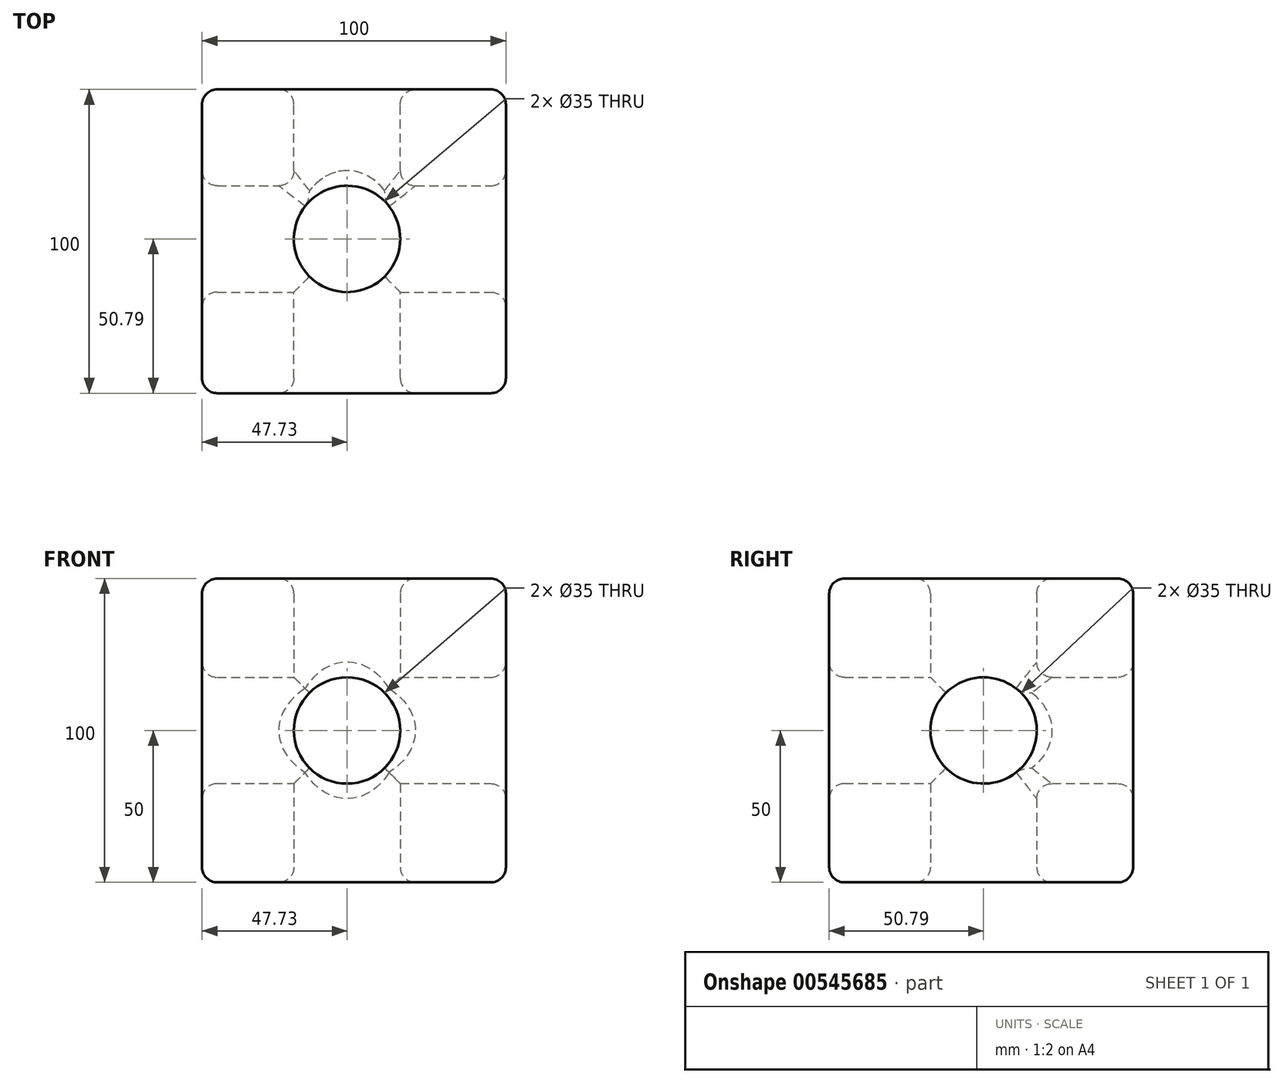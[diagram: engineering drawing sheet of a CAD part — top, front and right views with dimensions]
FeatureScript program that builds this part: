
annotation { "Feature Type Name" : "Feature", "Feature Type Description" : "" }
export const myFeature = defineFeature(function(context is Context, id is Id, definition is map)
    precondition{}
    {
        {
            var Q0;
            Q0=qCreatedBy(makeId("Top.planeOp"),FACE);
            var sketch = newSketch(context, id + "F0", { "sketchPlane" : qUnion([Q0])});
            skLineSegment(sketch, "E0.bottom", {"start": v(-47.73, -50.79) * mm, "end": v(52.27, -50.79) * mm});
            skLineSegment(sketch, "E0.top", {"start": v(-47.73, 49.21) * mm, "end": v(52.27, 49.21) * mm});
            skLineSegment(sketch, "E0.left", {"start": v(-47.73, -50.79) * mm, "end": v(-47.73, 49.21) * mm});
            skLineSegment(sketch, "E0.right", {"start": v(52.27, -50.79) * mm, "end": v(52.27, 49.21) * mm});
            skSolve(sketch);
        }
        {
            var Q0;
            Q0=makeQuery(id+"F0.imprint","IMPRINT",FACE,{"disambiguationData":[TD([[makeQuery(id+"F0.imprint","IMPRINT",EDGE,{"derivedFrom":sQuery(id+"F0.wireOp",EDGE,"E0.bottom")}),1.0]])]});
            extrude(context, id + "F1", {"entities" : qUnion([Q0]), "endBound" : BoundingType.SYMMETRIC, "depth" : 100 * mm, "offsetDistance" : 25 * mm});
        }
        {
            var Q0;
            Q0=makeQuery(id+"F1.opExtrude","CAP_FACE",FACE,{"disambiguationData":[OSD([sQuery(id+"F0.wireOp",EDGE,"E0.bottom"),sQuery(id+"F0.wireOp",EDGE,"E0.top"),sQuery(id+"F0.wireOp",EDGE,"E0.left"),sQuery(id+"F0.wireOp",EDGE,"E0.right")])],"isStart":true});
            var sketch = newSketch(context, id + "F2", { "sketchPlane" : qUnion([Q0])});
            skCircle(sketch, "E1", {"center": v(0, 0) * mm, "radius": 17.5 * mm});
            skSolve(sketch);
        }
        {
            var Q0;
            Q0=makeQuery(id+"F2.imprint","IMPRINT",FACE,{"disambiguationData":[TD([[makeQuery(id+"F2.imprint","IMPRINT",EDGE,{"derivedFrom":sQuery(id+"F2.wireOp",EDGE,"E1")}),1.0]])]});
            extrude(context, id + "F3", {"entities" : qUnion([Q0]), "operationType" : NewBodyOperationType.REMOVE, "endBound" : BoundingType.UP_TO_NEXT, "oppositeDirection" : true, "depth" : 25 * mm, "offsetDistance" : 25 * mm});
        }
        {
            var Q0;
            Q0=makeQuery(id+"F1.opExtrude","SWEPT_FACE",FACE,{"disambiguationData":[OSD([sQuery(id+"F0.wireOp",EDGE,"E0.right")])]});
            var sketch = newSketch(context, id + "F4", { "sketchPlane" : qUnion([Q0])});
            skCircle(sketch, "E2", {"center": v(0, 0) * mm, "radius": 17.5 * mm});
            skSolve(sketch);
        }
        {
            var Q0;
            Q0=makeQuery(id+"F4.imprint","IMPRINT",FACE,{"disambiguationData":[TD([[makeQuery(id+"F4.imprint","IMPRINT",EDGE,{"derivedFrom":sQuery(id+"F4.wireOp",EDGE,"E2")}),1.0]])]});
            extrude(context, id + "F5", {"entities" : qUnion([Q0]), "operationType" : NewBodyOperationType.REMOVE, "endBound" : BoundingType.THROUGH_ALL, "oppositeDirection" : true, "depth" : 25 * mm, "offsetDistance" : 25 * mm});
        }
        {
            var Q0;
            Q0=makeQuery(id+"F1.opExtrude","SWEPT_FACE",FACE,{"disambiguationData":[OSD([sQuery(id+"F0.wireOp",EDGE,"E0.top")])]});
            var sketch = newSketch(context, id + "F6", { "sketchPlane" : qUnion([Q0])});
            skCircle(sketch, "E3", {"center": v(0, 0) * mm, "radius": 17.5 * mm});
            skSolve(sketch);
        }
        {
            var Q0;
            Q0=makeQuery(id+"F6.imprint","IMPRINT",FACE,{"disambiguationData":[TD([[makeQuery(id+"F6.imprint","IMPRINT",EDGE,{"derivedFrom":sQuery(id+"F6.wireOp",EDGE,"E3")}),1.0]])]});
            extrude(context, id + "F7", {"entities" : qUnion([Q0]), "operationType" : NewBodyOperationType.REMOVE, "endBound" : BoundingType.THROUGH_ALL, "oppositeDirection" : true, "depth" : 25 * mm, "offsetDistance" : 25 * mm});
        }
        {
            var Q0;
            Q0=makeQuery(id+"F1.opExtrude","SWEPT_FACE",FACE,{"disambiguationData":[OSD([sQuery(id+"F0.wireOp",EDGE,"E0.right")])]});
            var Q1;
            Q1=makeQuery(id+"F1.opExtrude","CAP_EDGE",EDGE,{"disambiguationData":[OSD([sQuery(id+"F0.wireOp",EDGE,"E0.top")])],"isStart":false});
            var Q2;
            Q2=makeQuery(id+"F7.boolean.opBoolean","COPY",FACE,{"disambiguationData":[TD([makeQuery(id+"F1.opExtrude","SWEPT_FACE",FACE,{"disambiguationData":[OSD([sQuery(id+"F0.wireOp",EDGE,"E0.top")])]})])],"derivedFrom":makeQuery(id+"F7.opExtrude","SWEPT_FACE",FACE,{"disambiguationData":[OSD([sQuery(id+"F6.wireOp",EDGE,"E3")])]})});
            var Q3;
            Q3=makeQuery(id+"F1.opExtrude","CAP_FACE",FACE,{"disambiguationData":[OSD([sQuery(id+"F0.wireOp",EDGE,"E0.bottom"),sQuery(id+"F0.wireOp",EDGE,"E0.top"),sQuery(id+"F0.wireOp",EDGE,"E0.left"),sQuery(id+"F0.wireOp",EDGE,"E0.right")])],"isStart":true});
            var Q4;
            Q4=makeQuery(id+"F1.opExtrude","SWEPT_FACE",FACE,{"disambiguationData":[OSD([sQuery(id+"F0.wireOp",EDGE,"E0.left")])]});
            var Q5;
            Q5=makeQuery(id+"F1.opExtrude","SWEPT_FACE",FACE,{"disambiguationData":[OSD([sQuery(id+"F0.wireOp",EDGE,"E0.bottom")])]});
            var Q6;
            Q6=makeQuery(id+"F1.opExtrude","CAP_FACE",FACE,{"disambiguationData":[OSD([sQuery(id+"F0.wireOp",EDGE,"E0.bottom"),sQuery(id+"F0.wireOp",EDGE,"E0.top"),sQuery(id+"F0.wireOp",EDGE,"E0.left"),sQuery(id+"F0.wireOp",EDGE,"E0.right")])],"isStart":false});
            fillet(context, id + "F8", {"entities" : qUnion([Q0, Q1, Q2, Q3, Q4, Q5, Q6]), "radius" : 5 * mm, "tangentPropagation" : true, "allowEdgeOverflow" : false});
        }
    });
